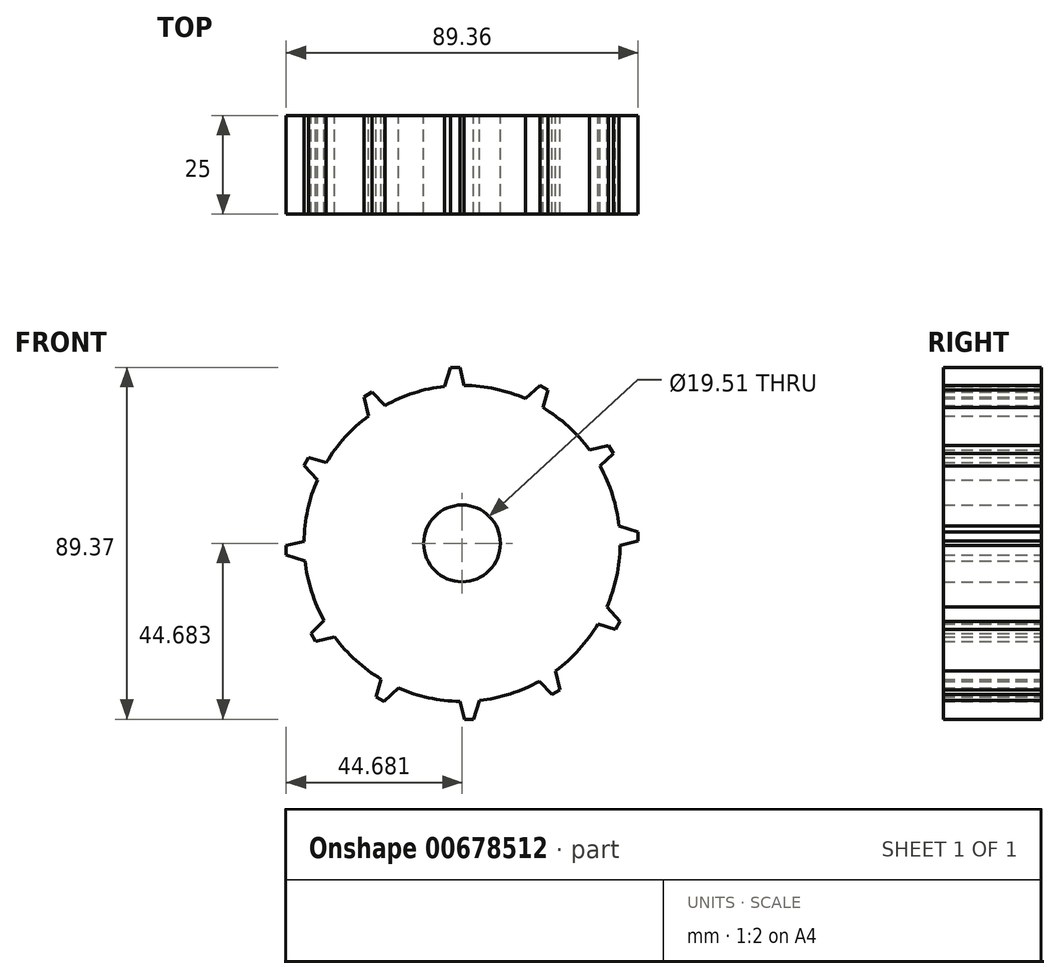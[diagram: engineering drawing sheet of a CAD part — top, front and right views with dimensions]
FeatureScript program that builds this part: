
annotation { "Feature Type Name" : "Feature", "Feature Type Description" : "" }
export const myFeature = defineFeature(function(context is Context, id is Id, definition is map)
    precondition{}
    {
        {
            var Q0;
            Q0=qCreatedBy(makeId("Front.planeOp"),FACE);
            var sketch = newSketch(context, id + "F0", { "sketchPlane" : qUnion([Q0])});
            skCircle(sketch, "E0", {"center": v(-4.86, 3.5) * mm, "radius": 26.86 * mm});
            skCircle(sketch, "E1", {"center": v(-4.86, 1.03) * mm, "radius": 29.34 * mm, "construction": true});
            skCircle(sketch, "E2", {"center": v(-4.86, 1.03) * mm, "radius": 31.75 * mm, "construction": true});
            skLineSegment(sketch, "E3", {"start": v(-4.86, 3.5) * mm, "end": v(-4.86, 60.6) * mm, "construction": true});
            skLineSegment(sketch, "E4", {"start": v(-4.86, 1.03) * mm, "end": v(-10.83, 92.13) * mm, "construction": true});
            skLineSegment(sketch, "E5", {"start": v(-4.86, 30.37) * mm, "end": v(-70.88, 37.9) * mm, "construction": true});
            skLineSegment(sketch, "E6", {"start": v(-4.86, 30.37) * mm, "end": v(-70.88, 14.54) * mm, "construction": true});
            skCircle(sketch, "E7", {"center": v(-4.86, 3.5) * mm, "radius": 26.12 * mm, "construction": true});
            skCircle(sketch, "E8", {"center": v(-4.86, 30.37) * mm, "radius": 7.3 * mm, "construction": true});
            skCircle(sketch, "E9", {"center": v(-11.96, 28.67) * mm, "radius": 7.3 * mm, "construction": true});
            skArc(sketch, "E10", {"start": v(-4.86, 30.37) * mm, "mid": v(-5.34, 31.6) * mm, "end": v(-5.92, 32.77) * mm});
            skLineSegment(sketch, "E11", {"start": v(-4.86, 30.37) * mm, "end": v(-4.86, 30.37) * mm});
            skArc(sketch, "E12.MirrorCS", {"start": v(-8.69, 30.12) * mm, "mid": v(-8.37, 31.4) * mm, "end": v(-7.95, 32.63) * mm});
            skLineSegment(sketch, "E13.MirrorCS", {"start": v(-8.69, 30.12) * mm, "end": v(-8.69, 30.12) * mm});
            skArc(sketch, "E14", {"start": v(-5.92, 32.77) * mm, "mid": v(1.15, 34.9) * mm, "end": v(7.01, 39.39) * mm});
            skLineSegment(sketch, "E15", {"start": v(-8.69, 30.12) * mm, "end": v(-8.7, 30.1) * mm});
            skArc(sketch, "E16", {"start": v(-4.86, 20.21) * mm, "mid": v(-5.49, 20.2) * mm, "end": v(-6.11, 20.17) * mm});
            skCircle(sketch, "E17", {"center": v(-4.86, 1.03) * mm, "radius": 40.15 * mm});
            skLineSegment(sketch, "E18.top", {"start": v(-6.44, 25.13) * mm, "end": v(-4.86, 25.13) * mm});
            skLineSegment(sketch, "E19", {"start": v(-9.25, 40.94) * mm, "end": v(-7.79, 45.72) * mm});
            skLineSegment(sketch, "E20", {"start": v(-7.79, 45.72) * mm, "end": v(-5.42, 45.72) * mm});
            skLineSegment(sketch, "E21", {"start": v(-5.42, 45.72) * mm, "end": v(-4.34, 41.18) * mm});
            skCircle(sketch, "E22", {"center": v(-4.86, 1.03) * mm, "radius": 9.75 * mm});
            skSolve(sketch);
        }
        {
            var Q0;
            Q0 = qSketchRegion(id + "F0", true);
            extrude(context, id + "F1", {"entities" : qUnion([Q0]), "depth" : 25 * mm, "offsetDistance" : 25 * mm});
        }
        {
            var Q0;
            {var subQ0=sQuery(id+"F0.wireOp",EDGE,"E0");var subQ1=makeQuery(id+"F0.imprint","IMPRINT",VERTEX,{"disambiguationData":[OD(0.0)],"derivedFrom":subQ0});Q0=makeQuery(id+"F0.imprint","IMPRINT",FACE,{"disambiguationData":[TD([[makeQuery(id+"F0.imprint","IMPRINT",EDGE,{"disambiguationData":[TD([[subQ1,-1.0]])],"derivedFrom":subQ0}),1.0]])]});}
            extrude(context, id + "F2", {"entities" : qUnion([Q0]), "operationType" : NewBodyOperationType.ADD, "depth" : 25 * mm, "offsetDistance" : 25 * mm});
        }
        {
            var Q0;
            Q0=makeQuery(id+"F1.opExtrude","SWEPT_BODY",BODY,{"disambiguationData":[OSD([sQuery(id+"F0.wireOp",EDGE,"E0"),sQuery(id+"F0.wireOp",EDGE,"E17"),sQuery(id+"F0.wireOp",EDGE,"E19"),sQuery(id+"F0.wireOp",EDGE,"E20"),sQuery(id+"F0.wireOp",EDGE,"E21")])]});
            var Q1;
            Q1=sQuery(id+"F0.wireOp",EDGE,"E2");
            circularPattern(context, id + "F3", {"operationType" : NewBodyOperationType.ADD, "entities" : qUnion([Q0]), "axis" : qUnion([Q1]), "angle" : 360 * degree, "instanceCount" : 12, "equalSpace" : true});
        }
    });
